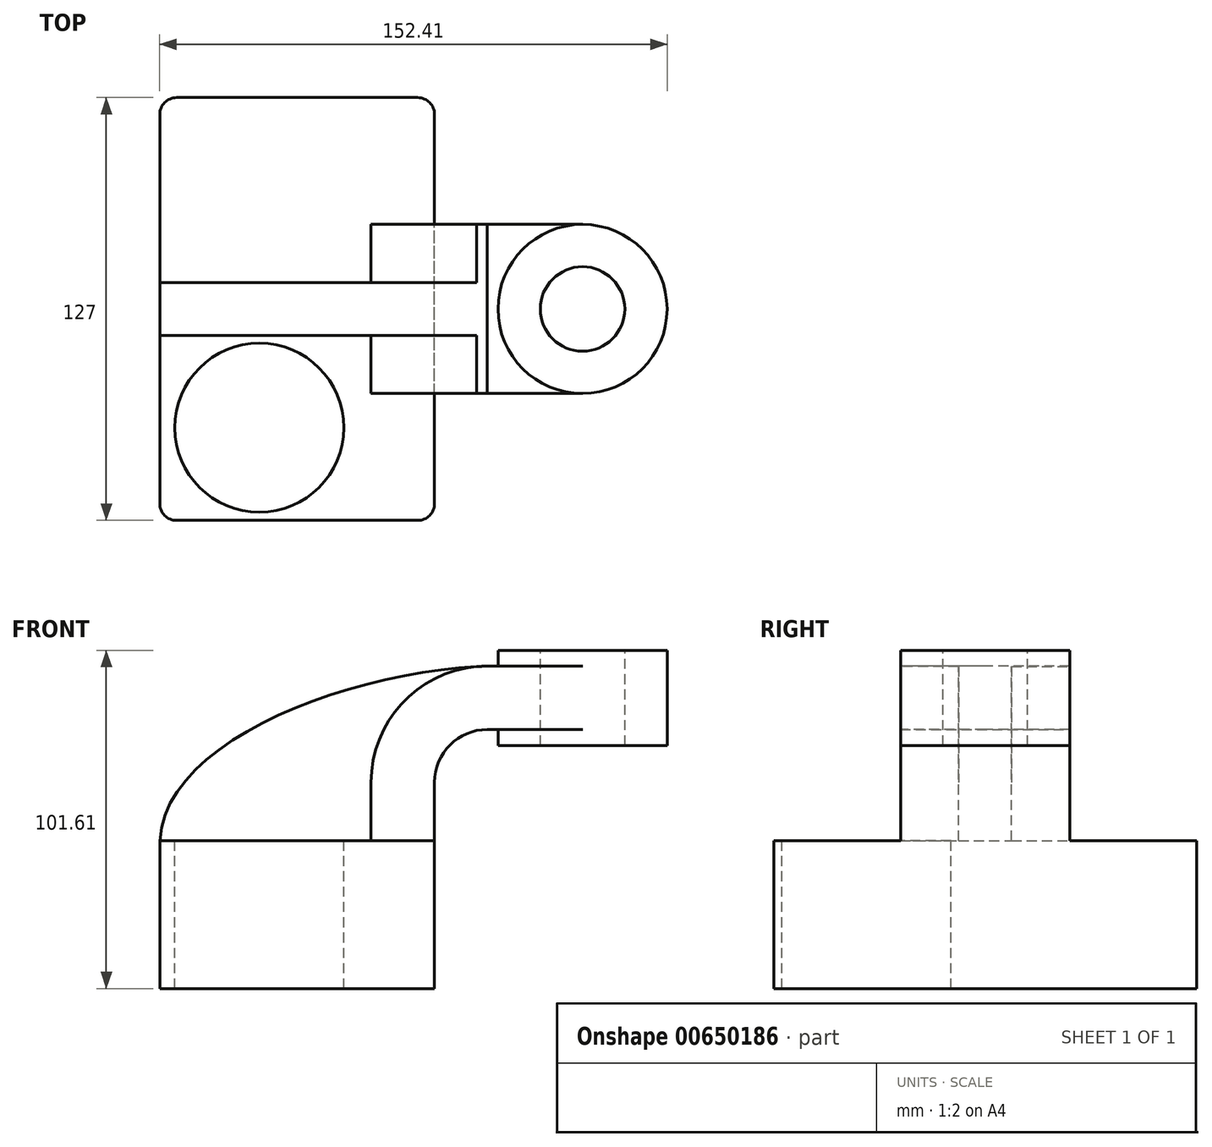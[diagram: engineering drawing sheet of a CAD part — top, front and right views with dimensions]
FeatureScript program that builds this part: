
annotation { "Feature Type Name" : "Feature", "Feature Type Description" : "" }
export const myFeature = defineFeature(function(context is Context, id is Id, definition is map)
    precondition{}
    {
        {
            var Q0;
            Q0=qCreatedBy(makeId("Front.planeOp"),FACE);
            var sketch = newSketch(context, id + "F0", { "sketchPlane" : qUnion([Q0])});
            skLineSegment(sketch, "E0.rect.bottom", {"start": v(-41.28, 9.52) * mm, "end": v(41.28, 9.52) * mm});
            skLineSegment(sketch, "E0.rect.top", {"start": v(-41.28, -9.52) * mm, "end": v(41.28, -9.52) * mm});
            skLineSegment(sketch, "E0.rect.left", {"start": v(-41.28, 9.52) * mm, "end": v(-41.28, -9.52) * mm});
            skLineSegment(sketch, "E0.rect.right", {"start": v(41.28, 9.52) * mm, "end": v(41.28, -9.52) * mm});
            skPoint(sketch, "E0.rect.middle", {"position": v(0, 0) * mm});
            skLineSegment(sketch, "E1", {"start": v(41.28, 9.52) * mm, "end": v(41.28, 27) * mm});
            skArc(sketch, "E2", {"start": v(41.28, 27) * mm, "mid": v(45.92, 38.23) * mm, "end": v(57.15, 42.88) * mm});
            skLineSegment(sketch, "E3", {"start": v(57.15, 42.88) * mm, "end": v(85.72, 42.88) * mm});
            skLineSegment(sketch, "E4.rect.bottom", {"start": v(60.32, 38.1) * mm, "end": v(111.12, 38.1) * mm});
            skLineSegment(sketch, "E4.rect.top", {"start": v(60.32, 66.68) * mm, "end": v(111.12, 66.68) * mm});
            skLineSegment(sketch, "E4.rect.left", {"start": v(60.32, 38.1) * mm, "end": v(60.32, 66.68) * mm});
            skLineSegment(sketch, "E4.rect.right", {"start": v(111.13, 38.1) * mm, "end": v(111.12, 66.68) * mm});
            skPoint(sketch, "E4.rect.middle", {"position": v(85.72, 52.39) * mm});
            skLineSegment(sketch, "E5.0", {"start": v(57.15, 61.93) * mm, "end": v(85.72, 61.93) * mm});
            skArc(sketch, "E5.1", {"start": v(22.23, 27) * mm, "mid": v(32.45, 51.7) * mm, "end": v(57.15, 61.93) * mm});
            skLineSegment(sketch, "E5.2", {"start": v(22.23, 9.52) * mm, "end": v(22.23, 27) * mm});
            skLineSegment(sketch, "E6", {"start": v(85.72, 38.1) * mm, "end": v(85.72, 66.68) * mm});
            skFitSpline(sketch, "E7", {"points": [v(-41.28, 9.53) * mm, v(57.15, 61.93) * mm], "startDerivative": vector(5.2, 92.34) * mm, "endDerivative": vector(120.92, 4.22) * mm});
            skSolve(sketch);
        }
        {
            var Q0;
            Q0=makeQuery(id+"F0.imprint","IMPRINT",FACE,{"disambiguationData":[TD([[makeQuery(id+"F0.imprint","IMPRINT",EDGE,{"derivedFrom":sQuery(id+"F0.wireOp",EDGE,"E0.rect.top")}),1.0]])]});
            extrude(context, id + "F1", {"entities" : qUnion([Q0]), "endBound" : BoundingType.SYMMETRIC, "depth" : 127 * mm});
        }
        {
            var Q0;
            {var subQ9=sQuery(id+"F0.wireOp",EDGE,"E1");Q0=makeQuery(id+"F0.imprint","IMPRINT",FACE,{"disambiguationData":[TD([[makeQuery(id+"F0.imprint","IMPRINT",EDGE,{"derivedFrom":subQ9}),1.0]])]});}
            var Q1;
            {var subQ0=sQuery(id+"F0.wireOp",EDGE,"E6");var subQ1=sQuery(id+"F0.wireOp",EDGE,"E3");var subQ2=makeQuery(id+"F0.imprint","INTERSECT",VERTEX,{"derivedFrom":[subQ1,subQ0]});Q1=makeQuery(id+"F0.imprint","IMPRINT",FACE,{"disambiguationData":[TD([[makeQuery(id+"F0.imprint","IMPRINT",EDGE,{"disambiguationData":[TD([[subQ2,1.0]])],"derivedFrom":subQ1}),1.0]])]});}
            extrude(context, id + "F2", {"entities" : qUnion([Q0, Q1]), "operationType" : NewBodyOperationType.ADD, "endBound" : BoundingType.SYMMETRIC, "depth" : 50.8 * mm});
        }
        {
            var Q0;
            {var subQ3=sQuery(id+"F0.wireOp",EDGE,"E5.2");Q0=makeQuery(id+"F0.imprint","IMPRINT",FACE,{"disambiguationData":[TD([[makeQuery(id+"F0.imprint","IMPRINT",EDGE,{"derivedFrom":subQ3}),1.0]])]});}
            extrude(context, id + "F3", {"entities" : qUnion([Q0]), "operationType" : NewBodyOperationType.ADD, "endBound" : BoundingType.SYMMETRIC, "depth" : 15.88 * mm});
        }
        {
            var Q0;
            {var subQ5=sQuery(id+"F0.wireOp",EDGE,"E4.rect.right");Q0=makeQuery(id+"F0.imprint","IMPRINT",FACE,{"disambiguationData":[TD([[makeQuery(id+"F0.imprint","IMPRINT",EDGE,{"derivedFrom":subQ5}),1.0]])]});}
            var Q1;
            Q1=sQuery(id+"F0.wireOp",EDGE,"E6");
            revolve(context, id + "F4", {"operationType" : NewBodyOperationType.ADD, "entities" : qUnion([Q0]), "axis" : qUnion([Q1]), "revolveType" : RevolveType.FULL});
        }
        {
            var Q0;
            Q0=makeQuery(id+"F1.opExtrude","CAP_EDGE",EDGE,{"disambiguationData":[OSD([sQuery(id+"F0.wireOp",EDGE,"E0.rect.right")])],"isStart":false});
            var Q1;
            Q1=makeQuery(id+"F1.opExtrude","CAP_EDGE",EDGE,{"disambiguationData":[OSD([sQuery(id+"F0.wireOp",EDGE,"E0.rect.left")])],"isStart":false});
            var Q2;
            Q2=makeQuery(id+"F1.opExtrude","CAP_EDGE",EDGE,{"disambiguationData":[OSD([sQuery(id+"F0.wireOp",EDGE,"E0.rect.right")])],"isStart":true});
            var Q3;
            Q3=makeQuery(id+"F1.opExtrude","CAP_EDGE",EDGE,{"disambiguationData":[OSD([sQuery(id+"F0.wireOp",EDGE,"E0.rect.left")])],"isStart":true});
            fillet(context, id + "F5", {"entities" : qUnion([Q0, Q1, Q2, Q3]), "radius" : 5.08 * mm, "tangentPropagation" : true, "allowEdgeOverflow" : false});
        }
        {
            var Q0;
            Q0=makeQuery(id+"F1.opExtrude","SWEPT_FACE",FACE,{"disambiguationData":[OSD([sQuery(id+"F0.wireOp",EDGE,"E0.rect.top")])]});
            extrude(context, id + "F6", {"entities" : qUnion([Q0]), "operationType" : NewBodyOperationType.ADD, "depth" : 25.4 * mm, "offsetDistance" : 25.4 * mm});
        }
        {
            var Q0;
            Q0=makeQuery(id+"F4.opRevolve","SWEPT_FACE",FACE,{"disambiguationData":[OSD([sQuery(id+"F0.wireOp",EDGE,"E4.rect.top")])]});
            var sketch = newSketch(context, id + "F7", { "sketchPlane" : qUnion([Q0])});
            skCircle(sketch, "E8", {"center": v(85.72, 0) * mm, "radius": 15.67 * mm});
            skSolve(sketch);
        }
        {
            var Q0;
            Q0=sQuery(id+"F7.wireOp",VERTEX,"E8.center");
            var Q1;
            Q1=makeQuery(id+"F1.opExtrude","SWEPT_BODY",BODY,{"disambiguationData":[OSD([sQuery(id+"F0.wireOp",EDGE,"E0.rect.bottom"),sQuery(id+"F0.wireOp",EDGE,"E0.rect.top"),sQuery(id+"F0.wireOp",EDGE,"E0.rect.left"),sQuery(id+"F0.wireOp",EDGE,"E0.rect.right")])]});
            hole(context, id + "F8", {"style" : HoleStyle.SIMPLE, "endStyle" : HoleEndStyle.THROUGH, "holeDiameter" : 25.4 * mm, "majorDiameter" : 6.35 * mm, "isTappedThrough" : true, "tappedDepth" : 12.7 * mm, "tapClearance" : 3, "locations" : qUnion([Q0]), "scope" : qUnion([Q1])});
        }
        {
            var Q0;
            {var subQ4=sQuery(id+"F0.wireOp",EDGE,"E0.rect.bottom");var subQ5=sQuery(id+"F0.wireOp",EDGE,"E0.rect.right");var subQ6=sQuery(id+"F0.wireOp",EDGE,"E0.rect.left");Q0=makeQuery(id+"F3.boolean.opBoolean","SPLIT",FACE,{"disambiguationData":[TD([makeQuery(id+"F1.opExtrude","CAP_FACE",FACE,{"disambiguationData":[OSD([subQ4,sQuery(id+"F0.wireOp",EDGE,"E0.rect.top"),subQ6,subQ5])],"isStart":false})])],"derivedFrom":makeQuery(id+"F1.opExtrude","SWEPT_FACE",FACE,{"disambiguationData":[OSD([subQ4])]})});}
            var sketch = newSketch(context, id + "F9", { "sketchPlane" : qUnion([Q0])});
            skPoint(sketch, "E9", {"position": v(-11.36, -35.65) * mm});
            skSolve(sketch);
        }
        {
            var Q0;
            Q0=sQuery(id+"F9.wireOp",VERTEX,"E9");
            var Q1;
            Q1=makeQuery(id+"F1.opExtrude","SWEPT_BODY",BODY,{"disambiguationData":[OSD([sQuery(id+"F0.wireOp",EDGE,"E0.rect.bottom"),sQuery(id+"F0.wireOp",EDGE,"E0.rect.top"),sQuery(id+"F0.wireOp",EDGE,"E0.rect.left"),sQuery(id+"F0.wireOp",EDGE,"E0.rect.right")])]});
            hole(context, id + "F10", {"style" : HoleStyle.SIMPLE, "endStyle" : HoleEndStyle.THROUGH, "holeDiameter" : 50.8 * mm, "majorDiameter" : 6.35 * mm, "isTappedThrough" : true, "tappedDepth" : 12.7 * mm, "tapClearance" : 3, "locations" : qUnion([Q0]), "scope" : qUnion([Q1])});
        }
    });
